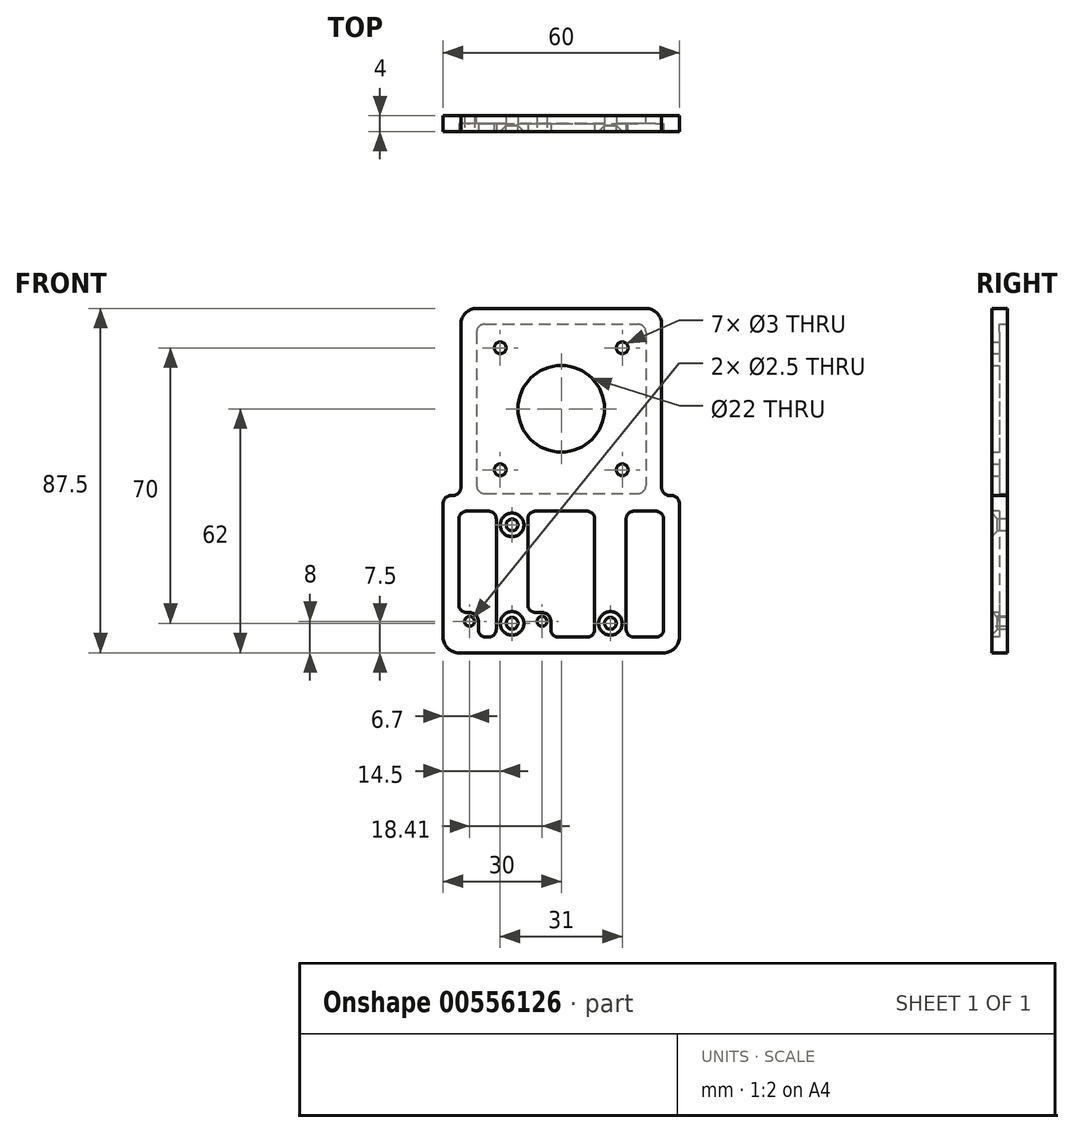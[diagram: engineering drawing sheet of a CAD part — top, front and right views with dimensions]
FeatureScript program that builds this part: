
annotation { "Feature Type Name" : "Feature", "Feature Type Description" : "" }
export const myFeature = defineFeature(function(context is Context, id is Id, definition is map)
    precondition{}
    {
        {
            var Q0;
            Q0=qCreatedBy(makeId("Front.planeOp"),FACE);
            var sketch = newSketch(context, id + "F0", { "sketchPlane" : qUnion([Q0])});
            skPoint(sketch, "E0.middle", {"position": v(0, 0) * mm});
            skLineSegment(sketch, "E1.bottom", {"start": v(21, 41) * mm, "end": v(-21, 41) * mm, "construction": true});
            skLineSegment(sketch, "E1.top", {"start": v(21, -1) * mm, "end": v(-21, -1) * mm, "construction": true});
            skLineSegment(sketch, "E1.left", {"start": v(21, 41) * mm, "end": v(21, -1) * mm, "construction": true});
            skLineSegment(sketch, "E1.right", {"start": v(-21, 41) * mm, "end": v(-21, -1) * mm, "construction": true});
            skPoint(sketch, "E1.middle", {"position": v(0, 20) * mm});
            skLineSegment(sketch, "E2.left", {"start": v(30, -2) * mm, "end": v(30, -42) * mm, "construction": true});
            skLineSegment(sketch, "E2.right", {"start": v(-30, -2) * mm, "end": v(-30, -42) * mm, "construction": true});
            skPoint(sketch, "E2.middle", {"position": v(0, -22) * mm});
            skLineSegment(sketch, "E3", {"start": v(-25.5, -2) * mm, "end": v(-25.5, 45.5) * mm});
            skLineSegment(sketch, "E4", {"start": v(25.5, -2) * mm, "end": v(25.5, 45.5) * mm});
            skLineSegment(sketch, "E5", {"start": v(-25.5, 45.5) * mm, "end": v(25.5, 45.5) * mm});
            skLineSegment(sketch, "E6", {"start": v(-30, -2) * mm, "end": v(-30, -42) * mm});
            skLineSegment(sketch, "E7", {"start": v(30, -42) * mm, "end": v(30, -2) * mm});
            skLineSegment(sketch, "E8", {"start": v(30, -42) * mm, "end": v(-30, -42) * mm});
            skLineSegment(sketch, "E9", {"start": v(-30, -2) * mm, "end": v(30, -2) * mm});
            skSolve(sketch);
        }
        {
            var Q0;
            Q0 = qSketchRegion(id + "F0", true);
            extrude(context, id + "F1", {"entities" : qUnion([Q0]), "depth" : 4 * mm, "offsetDistance" : 25 * mm});
        }
        {
            var Q0;
            Q0=makeQuery(id+"F1.opExtrude","CAP_FACE",FACE,{"disambiguationData":[OSD([sQuery(id+"F0.wireOp",EDGE,"E3"),sQuery(id+"F0.wireOp",EDGE,"E4"),sQuery(id+"F0.wireOp",EDGE,"AjVsnIKu-7JX5-ZN3J-yJHr-BJJlj0IjsVSh"),sQuery(id+"F0.wireOp",EDGE,"zUF1eDCT-iJ0q-WYJ5-TO9I-DUBJJ4F8TYCG"),sQuery(id+"F0.wireOp",EDGE,"R0gw3s5Z-myCC-VoIE-qQNj-JX5kTqaqAvmN"),sQuery(id+"F0.wireOp",EDGE,"0TTXeeu4-dUPo-6RlB-0m7P-MXHo5uVCwiDz"),sQuery(id+"F0.wireOp",EDGE,"BTNMlOGm-kpXo-JoPY-6Hj9-Lp1ODQrAF4Rl"),sQuery(id+"F0.wireOp",EDGE,"W4vJ1xEX-BTs7-1cIY-8ppp-jU2IqAzzoPHu"),sQuery(id+"F0.wireOp",EDGE,"rjm4BpMY-it7c-iU0h-PZAg-QSvS56OCM9jP"),sQuery(id+"F0.wireOp",EDGE,"aUghs46N-WyLj-duN1-bhaf-177DD2MuhRqQ"),sQuery(id+"F0.wireOp",EDGE,"JDqdSihL-KQaK-Av0N-iznf-jRKgxYS6iGmx"),sQuery(id+"F0.wireOp",EDGE,"zwNCGtTh-hdHv-TKGf-VZcB-xR8iGKQpC6Up"),sQuery(id+"F0.wireOp",EDGE,"Ke8YQDsO-ZVhX-azsC-oTJZ-QnQdDkfL8EHA"),sQuery(id+"F0.wireOp",EDGE,"E5"),sQuery(id+"F0.wireOp",EDGE,"p4yK42dh-cCTi-oaBX-tSVU-OnHXovtltKjl"),sQuery(id+"F0.wireOp",EDGE,"P8wBvtXH-8kAn-NcBt-zPsC-BQHUZ9UxVdzU"),sQuery(id+"F0.wireOp",EDGE,"E6"),sQuery(id+"F0.wireOp",EDGE,"E7"),sQuery(id+"F0.wireOp",EDGE,"nOxL5zSL-pdkV-Zte1-GYdC-ii0rABZTziLy"),sQuery(id+"F0.wireOp",EDGE,"9Hkm7kCb-Kjb3-Cx3j-kGQn-9n4TcQlOuVeR")])],"isStart":true});
            var sketch = newSketch(context, id + "F2", { "sketchPlane" : qUnion([Q0])});
            skLineSegment(sketch, "E10.bottom", {"start": v(21.5, 41.5) * mm, "end": v(-21.5, 41.5) * mm});
            skLineSegment(sketch, "E10.top", {"start": v(21.5, -1.5) * mm, "end": v(-21.5, -1.5) * mm});
            skLineSegment(sketch, "E10.left", {"start": v(21.5, 41.5) * mm, "end": v(21.5, -1.5) * mm});
            skLineSegment(sketch, "E10.right", {"start": v(-21.5, 41.5) * mm, "end": v(-21.5, -1.5) * mm});
            skLineSegment(sketch, "E11.bottom", {"start": v(15.5, 35.5) * mm, "end": v(-15.5, 35.5) * mm, "construction": true});
            skLineSegment(sketch, "E11.top", {"start": v(15.5, 4.5) * mm, "end": v(-15.5, 4.5) * mm, "construction": true});
            skLineSegment(sketch, "E11.left", {"start": v(15.5, 35.5) * mm, "end": v(15.5, 4.5) * mm, "construction": true});
            skLineSegment(sketch, "E11.right", {"start": v(-15.5, 35.5) * mm, "end": v(-15.5, 4.5) * mm, "construction": true});
            skPoint(sketch, "E11.middle", {"position": v(0, 20) * mm});
            skCircle(sketch, "E12", {"center": v(0, 20) * mm, "radius": 11 * mm});
            skSolve(sketch);
        }
        {
            var Q0;
            Q0=makeQuery(id+"F2.imprint","IMPRINT",FACE,{"disambiguationData":[TD([[makeQuery(id+"F2.imprint","IMPRINT",EDGE,{"derivedFrom":sQuery(id+"F2.wireOp",EDGE,"E10.bottom")}),1.0]])]});
            extrude(context, id + "F3", {"entities" : qUnion([Q0]), "operationType" : NewBodyOperationType.REMOVE, "oppositeDirection" : true, "depth" : 2 * mm, "offsetDistance" : 25 * mm});
        }
        {
            var Q0;
            Q0=makeQuery(id+"F2.imprint","IMPRINT",FACE,{"disambiguationData":[TD([[makeQuery(id+"F2.imprint","IMPRINT",EDGE,{"derivedFrom":sQuery(id+"F2.wireOp",EDGE,"E12")}),1.0]])]});
            extrude(context, id + "F4", {"entities" : qUnion([Q0]), "operationType" : NewBodyOperationType.REMOVE, "endBound" : BoundingType.THROUGH_ALL, "oppositeDirection" : true, "depth" : 25 * mm, "offsetDistance" : 25 * mm});
        }
        {
            var Q0;
            Q0=sQuery(id+"F2.wireOp",VERTEX,"E11.right.start");
            var Q1;
            Q1=sQuery(id+"F2.wireOp",VERTEX,"E11.left.start");
            var Q2;
            Q2=sQuery(id+"F2.wireOp",VERTEX,"E11.top.start");
            var Q3;
            Q3=sQuery(id+"F2.wireOp",VERTEX,"E11.right.end");
            var Q4;
            Q4=makeQuery(id+"F1.opExtrude","SWEPT_BODY",BODY,{"disambiguationData":[OSD([sQuery(id+"F0.wireOp",EDGE,"E3"),sQuery(id+"F0.wireOp",EDGE,"E4"),sQuery(id+"F0.wireOp",EDGE,"AjVsnIKu-7JX5-ZN3J-yJHr-BJJlj0IjsVSh"),sQuery(id+"F0.wireOp",EDGE,"zUF1eDCT-iJ0q-WYJ5-TO9I-DUBJJ4F8TYCG"),sQuery(id+"F0.wireOp",EDGE,"R0gw3s5Z-myCC-VoIE-qQNj-JX5kTqaqAvmN"),sQuery(id+"F0.wireOp",EDGE,"0TTXeeu4-dUPo-6RlB-0m7P-MXHo5uVCwiDz"),sQuery(id+"F0.wireOp",EDGE,"BTNMlOGm-kpXo-JoPY-6Hj9-Lp1ODQrAF4Rl"),sQuery(id+"F0.wireOp",EDGE,"W4vJ1xEX-BTs7-1cIY-8ppp-jU2IqAzzoPHu"),sQuery(id+"F0.wireOp",EDGE,"rjm4BpMY-it7c-iU0h-PZAg-QSvS56OCM9jP"),sQuery(id+"F0.wireOp",EDGE,"aUghs46N-WyLj-duN1-bhaf-177DD2MuhRqQ"),sQuery(id+"F0.wireOp",EDGE,"JDqdSihL-KQaK-Av0N-iznf-jRKgxYS6iGmx"),sQuery(id+"F0.wireOp",EDGE,"zwNCGtTh-hdHv-TKGf-VZcB-xR8iGKQpC6Up"),sQuery(id+"F0.wireOp",EDGE,"Ke8YQDsO-ZVhX-azsC-oTJZ-QnQdDkfL8EHA"),sQuery(id+"F0.wireOp",EDGE,"E5"),sQuery(id+"F0.wireOp",EDGE,"p4yK42dh-cCTi-oaBX-tSVU-OnHXovtltKjl"),sQuery(id+"F0.wireOp",EDGE,"P8wBvtXH-8kAn-NcBt-zPsC-BQHUZ9UxVdzU"),sQuery(id+"F0.wireOp",EDGE,"E6"),sQuery(id+"F0.wireOp",EDGE,"E7"),sQuery(id+"F0.wireOp",EDGE,"nOxL5zSL-pdkV-Zte1-GYdC-ii0rABZTziLy"),sQuery(id+"F0.wireOp",EDGE,"9Hkm7kCb-Kjb3-Cx3j-kGQn-9n4TcQlOuVeR")])]});
            hole(context, id + "F5", {"style" : HoleStyle.SIMPLE, "endStyle" : HoleEndStyle.THROUGH, "holeDiameter" : 3 * mm, "majorDiameter" : 5 * mm, "isTappedThrough" : true, "tappedDepth" : 12 * mm, "tapClearance" : 3, "locations" : qUnion([Q0, Q1, Q2, Q3]), "scope" : qUnion([Q4])});
        }
        {
            var Q0;
            Q0=makeQuery(id+"F3.boolean.opBoolean","COPY",EDGE,{"derivedFrom":makeQuery(id+"F3.opExtrude","SWEPT_EDGE",EDGE,{"disambiguationData":[OSD([sQuery(id+"F2.wireOp",EDGE,"E10.bottom"),sQuery(id+"F2.wireOp",EDGE,"E10.right")])]})});
            var Q1;
            Q1=makeQuery(id+"F3.boolean.opBoolean","COPY",EDGE,{"derivedFrom":makeQuery(id+"F3.opExtrude","SWEPT_EDGE",EDGE,{"disambiguationData":[OSD([sQuery(id+"F2.wireOp",EDGE,"E10.bottom"),sQuery(id+"F2.wireOp",EDGE,"E10.left")])]})});
            var Q2;
            Q2=makeQuery(id+"F3.boolean.opBoolean","COPY",EDGE,{"derivedFrom":makeQuery(id+"F3.opExtrude","SWEPT_EDGE",EDGE,{"disambiguationData":[OSD([sQuery(id+"F2.wireOp",EDGE,"E10.top"),sQuery(id+"F2.wireOp",EDGE,"E10.left")])]})});
            var Q3;
            Q3=makeQuery(id+"F3.boolean.opBoolean","COPY",EDGE,{"derivedFrom":makeQuery(id+"F3.opExtrude","SWEPT_EDGE",EDGE,{"disambiguationData":[OSD([sQuery(id+"F2.wireOp",EDGE,"E10.top"),sQuery(id+"F2.wireOp",EDGE,"E10.right")])]})});
            fillet(context, id + "F6", {"entities" : qUnion([Q0, Q1, Q2, Q3]), "radius" : 2 * mm, "tangentPropagation" : true, "allowEdgeOverflow" : false});
        }
        {
            var Q0;
            Q0=makeQuery(id+"F1.opExtrude","CAP_FACE",FACE,{"disambiguationData":[OSD([sQuery(id+"F0.wireOp",EDGE,"E3"),sQuery(id+"F0.wireOp",EDGE,"E4"),sQuery(id+"F0.wireOp",EDGE,"AjVsnIKu-7JX5-ZN3J-yJHr-BJJlj0IjsVSh"),sQuery(id+"F0.wireOp",EDGE,"zUF1eDCT-iJ0q-WYJ5-TO9I-DUBJJ4F8TYCG"),sQuery(id+"F0.wireOp",EDGE,"R0gw3s5Z-myCC-VoIE-qQNj-JX5kTqaqAvmN"),sQuery(id+"F0.wireOp",EDGE,"0TTXeeu4-dUPo-6RlB-0m7P-MXHo5uVCwiDz"),sQuery(id+"F0.wireOp",EDGE,"BTNMlOGm-kpXo-JoPY-6Hj9-Lp1ODQrAF4Rl"),sQuery(id+"F0.wireOp",EDGE,"W4vJ1xEX-BTs7-1cIY-8ppp-jU2IqAzzoPHu"),sQuery(id+"F0.wireOp",EDGE,"rjm4BpMY-it7c-iU0h-PZAg-QSvS56OCM9jP"),sQuery(id+"F0.wireOp",EDGE,"aUghs46N-WyLj-duN1-bhaf-177DD2MuhRqQ"),sQuery(id+"F0.wireOp",EDGE,"JDqdSihL-KQaK-Av0N-iznf-jRKgxYS6iGmx"),sQuery(id+"F0.wireOp",EDGE,"zwNCGtTh-hdHv-TKGf-VZcB-xR8iGKQpC6Up"),sQuery(id+"F0.wireOp",EDGE,"Ke8YQDsO-ZVhX-azsC-oTJZ-QnQdDkfL8EHA"),sQuery(id+"F0.wireOp",EDGE,"E5"),sQuery(id+"F0.wireOp",EDGE,"p4yK42dh-cCTi-oaBX-tSVU-OnHXovtltKjl"),sQuery(id+"F0.wireOp",EDGE,"P8wBvtXH-8kAn-NcBt-zPsC-BQHUZ9UxVdzU"),sQuery(id+"F0.wireOp",EDGE,"E6"),sQuery(id+"F0.wireOp",EDGE,"E7"),sQuery(id+"F0.wireOp",EDGE,"nOxL5zSL-pdkV-Zte1-GYdC-ii0rABZTziLy"),sQuery(id+"F0.wireOp",EDGE,"9Hkm7kCb-Kjb3-Cx3j-kGQn-9n4TcQlOuVeR")])],"isStart":false});
            var sketch = newSketch(context, id + "F7", { "sketchPlane" : qUnion([Q0])});
            skLineSegment(sketch, "E13.bottom", {"start": v(-12.5, -9.5) * mm, "end": v(12.5, -9.5) * mm, "construction": true});
            skLineSegment(sketch, "E13.top", {"start": v(12.5, -34.5) * mm, "end": v(-12.5, -34.5) * mm, "construction": true});
            skLineSegment(sketch, "E13.left", {"start": v(12.5, -9.5) * mm, "end": v(12.5, -34.5) * mm, "construction": true});
            skLineSegment(sketch, "E13.right", {"start": v(-12.5, -9.5) * mm, "end": v(-12.5, -34.5) * mm, "construction": true});
            skPoint(sketch, "E13.middle", {"position": v(0, -22) * mm});
            skLineSegment(sketch, "E14.bottom", {"start": v(26, -6) * mm, "end": v(-26, -6) * mm});
            skLineSegment(sketch, "E14.top", {"start": v(26, -38) * mm, "end": v(-26, -38) * mm});
            skLineSegment(sketch, "E14.left", {"start": v(26, -6) * mm, "end": v(26, -38) * mm});
            skLineSegment(sketch, "E14.right", {"start": v(-26, -6) * mm, "end": v(-26, -38) * mm});
            skLineSegment(sketch, "E15", {"start": v(-23.3, -34) * mm, "end": v(-4.9, -34) * mm, "construction": true});
            skCircle(sketch, "E16", {"center": v(-23.3, -34) * mm, "radius": 2.25 * mm});
            skCircle(sketch, "E17", {"center": v(-4.9, -34) * mm, "radius": 2.25 * mm});
            skLineSegment(sketch, "E18", {"start": v(-26, -31.75) * mm, "end": v(-23.3, -31.75) * mm});
            skLineSegment(sketch, "E19", {"start": v(-21.05, -34) * mm, "end": v(-21.05, -38) * mm});
            skLineSegment(sketch, "E20", {"start": v(-2.64, -34) * mm, "end": v(-2.64, -38) * mm});
            skLineSegment(sketch, "E21.bottom", {"start": v(-8.5, -6) * mm, "end": v(-16.5, -6) * mm});
            skLineSegment(sketch, "E21.top", {"start": v(-8.5, -38) * mm, "end": v(-16.5, -38) * mm});
            skLineSegment(sketch, "E21.left", {"start": v(-8.5, -6) * mm, "end": v(-8.5, -38) * mm});
            skLineSegment(sketch, "E21.right", {"start": v(-16.5, -6) * mm, "end": v(-16.5, -38) * mm});
            skPoint(sketch, "E21.middle", {"position": v(-12.5, -22) * mm});
            skLineSegment(sketch, "E22.bottom", {"start": v(16.5, -6) * mm, "end": v(8.5, -6) * mm});
            skLineSegment(sketch, "E22.top", {"start": v(16.5, -38) * mm, "end": v(8.5, -38) * mm});
            skLineSegment(sketch, "E22.left", {"start": v(16.5, -6) * mm, "end": v(16.5, -38) * mm});
            skLineSegment(sketch, "E22.right", {"start": v(8.5, -6) * mm, "end": v(8.5, -38) * mm});
            skPoint(sketch, "E22.middle", {"position": v(12.5, -22) * mm});
            skLineSegment(sketch, "E23", {"start": v(-4.9, -31.75) * mm, "end": v(-8.5, -31.75) * mm});
            skSolve(sketch);
        }
        {
            var Q0;
            {var subQ3=sQuery(id+"F7.wireOp",EDGE,"E18");Q0=makeQuery(id+"F7.imprint","IMPRINT",FACE,{"disambiguationData":[TD([[makeQuery(id+"F7.imprint","IMPRINT",EDGE,{"derivedFrom":subQ3}),1.0]])]});}
            var Q1;
            {var subQ0=sQuery(id+"F7.wireOp",EDGE,"E20");Q1=makeQuery(id+"F7.imprint","IMPRINT",FACE,{"disambiguationData":[TD([[makeQuery(id+"F7.imprint","IMPRINT",EDGE,{"derivedFrom":subQ0}),1.0]])]});}
            var Q2;
            {var subQ0=sQuery(id+"F7.wireOp",EDGE,"E14.left");Q2=makeQuery(id+"F7.imprint","IMPRINT",FACE,{"disambiguationData":[TD([[makeQuery(id+"F7.imprint","IMPRINT",EDGE,{"derivedFrom":subQ0}),-1.0]])]});}
            extrude(context, id + "F8", {"entities" : qUnion([Q0, Q1, Q2]), "operationType" : NewBodyOperationType.REMOVE, "oppositeDirection" : true, "depth" : 2 * mm, "offsetDistance" : 25 * mm});
        }
        {
            var Q0;
            Q0=sQuery(id+"F7.wireOp",VERTEX,"E13.right.start");
            var Q1;
            Q1=sQuery(id+"F7.wireOp",VERTEX,"E13.bottom.start");
            var Q2;
            Q2=sQuery(id+"F7.wireOp",VERTEX,"E13.top.end");
            var Q3;
            Q3=sQuery(id+"F7.wireOp",VERTEX,"E13.left.end");
            var Q4;
            Q4=makeQuery(id+"F1.opExtrude","SWEPT_BODY",BODY,{"disambiguationData":[OSD([sQuery(id+"F0.wireOp",EDGE,"E3"),sQuery(id+"F0.wireOp",EDGE,"E4"),sQuery(id+"F0.wireOp",EDGE,"AjVsnIKu-7JX5-ZN3J-yJHr-BJJlj0IjsVSh"),sQuery(id+"F0.wireOp",EDGE,"zUF1eDCT-iJ0q-WYJ5-TO9I-DUBJJ4F8TYCG"),sQuery(id+"F0.wireOp",EDGE,"R0gw3s5Z-myCC-VoIE-qQNj-JX5kTqaqAvmN"),sQuery(id+"F0.wireOp",EDGE,"0TTXeeu4-dUPo-6RlB-0m7P-MXHo5uVCwiDz"),sQuery(id+"F0.wireOp",EDGE,"BTNMlOGm-kpXo-JoPY-6Hj9-Lp1ODQrAF4Rl"),sQuery(id+"F0.wireOp",EDGE,"W4vJ1xEX-BTs7-1cIY-8ppp-jU2IqAzzoPHu"),sQuery(id+"F0.wireOp",EDGE,"rjm4BpMY-it7c-iU0h-PZAg-QSvS56OCM9jP"),sQuery(id+"F0.wireOp",EDGE,"aUghs46N-WyLj-duN1-bhaf-177DD2MuhRqQ"),sQuery(id+"F0.wireOp",EDGE,"JDqdSihL-KQaK-Av0N-iznf-jRKgxYS6iGmx"),sQuery(id+"F0.wireOp",EDGE,"zwNCGtTh-hdHv-TKGf-VZcB-xR8iGKQpC6Up"),sQuery(id+"F0.wireOp",EDGE,"Ke8YQDsO-ZVhX-azsC-oTJZ-QnQdDkfL8EHA"),sQuery(id+"F0.wireOp",EDGE,"E5"),sQuery(id+"F0.wireOp",EDGE,"p4yK42dh-cCTi-oaBX-tSVU-OnHXovtltKjl"),sQuery(id+"F0.wireOp",EDGE,"P8wBvtXH-8kAn-NcBt-zPsC-BQHUZ9UxVdzU"),sQuery(id+"F0.wireOp",EDGE,"E6"),sQuery(id+"F0.wireOp",EDGE,"E7"),sQuery(id+"F0.wireOp",EDGE,"nOxL5zSL-pdkV-Zte1-GYdC-ii0rABZTziLy"),sQuery(id+"F0.wireOp",EDGE,"9Hkm7kCb-Kjb3-Cx3j-kGQn-9n4TcQlOuVeR")])]});
            hole(context, id + "F9", {"style" : HoleStyle.C_SINK, "endStyle" : HoleEndStyle.THROUGH, "holeDiameter" : 3 * mm, "cSinkDiameter" : 6 * mm, "cSinkAngle" : 90 * degree, "majorDiameter" : 5 * mm, "isTappedThrough" : true, "tappedDepth" : 12 * mm, "tapClearance" : 3, "startFromSketch" : true, "locations" : qUnion([Q0, Q1, Q2, Q3]), "scope" : qUnion([Q4])});
        }
        {
            var Q0;
            Q0=sQuery(id+"F7.wireOp",VERTEX,"E16.center");
            var Q1;
            Q1=sQuery(id+"F7.wireOp",VERTEX,"E15.end");
            var Q2;
            Q2=makeQuery(id+"F1.opExtrude","SWEPT_BODY",BODY,{"disambiguationData":[OSD([sQuery(id+"F0.wireOp",EDGE,"E3"),sQuery(id+"F0.wireOp",EDGE,"E4"),sQuery(id+"F0.wireOp",EDGE,"E5"),sQuery(id+"F0.wireOp",EDGE,"E6"),sQuery(id+"F0.wireOp",EDGE,"E7"),sQuery(id+"F0.wireOp",EDGE,"E8"),sQuery(id+"F0.wireOp",EDGE,"E9")])]});
            hole(context, id + "F10", {"style" : HoleStyle.SIMPLE, "endStyle" : HoleEndStyle.THROUGH, "holeDiameter" : 2.5 * mm, "majorDiameter" : 5 * mm, "isTappedThrough" : true, "tappedDepth" : 12 * mm, "tapClearance" : 3, "locations" : qUnion([Q0, Q1]), "scope" : qUnion([Q2])});
        }
        {
            var Q0;
            Q0=makeQuery(id+"F8.boolean.opBoolean","COPY",EDGE,{"derivedFrom":makeQuery(id+"F8.opExtrude","SWEPT_EDGE",EDGE,{"disambiguationData":[OSD([sQuery(id+"F7.wireOp",EDGE,"E14.bottom"),sQuery(id+"F7.wireOp",EDGE,"E14.right")])]})});
            var Q1;
            Q1=makeQuery(id+"F8.boolean.opBoolean","COPY",EDGE,{"derivedFrom":makeQuery(id+"F8.opExtrude","SWEPT_EDGE",EDGE,{"disambiguationData":[OSD([sQuery(id+"F7.wireOp",EDGE,"E14.bottom"),sQuery(id+"F7.wireOp",EDGE,"E14.left")])]})});
            var Q2;
            Q2=makeQuery(id+"F8.boolean.opBoolean","COPY",EDGE,{"derivedFrom":makeQuery(id+"F8.opExtrude","SWEPT_EDGE",EDGE,{"disambiguationData":[OSD([sQuery(id+"F7.wireOp",EDGE,"E14.top"),sQuery(id+"F7.wireOp",EDGE,"E14.right")])]})});
            var Q3;
            Q3=makeQuery(id+"F8.boolean.opBoolean","COPY",EDGE,{"derivedFrom":makeQuery(id+"F8.opExtrude","SWEPT_EDGE",EDGE,{"disambiguationData":[OSD([sQuery(id+"F7.wireOp",EDGE,"E14.top"),sQuery(id+"F7.wireOp",EDGE,"E14.left")])]})});
            var Q4;
            Q4=makeQuery(id+"F8.boolean.opBoolean","COPY",EDGE,{"derivedFrom":makeQuery(id+"F8.opExtrude","SWEPT_EDGE",EDGE,{"disambiguationData":[OSD([sQuery(id+"F7.wireOp",EDGE,"E14.top"),sQuery(id+"F7.wireOp",EDGE,"E21.top"),sQuery(id+"F7.wireOp",EDGE,"E21.right")])]})});
            var Q5;
            Q5=makeQuery(id+"F8.boolean.opBoolean","COPY",EDGE,{"derivedFrom":makeQuery(id+"F8.opExtrude","SWEPT_EDGE",EDGE,{"disambiguationData":[OSD([sQuery(id+"F7.wireOp",EDGE,"E14.top"),sQuery(id+"F7.wireOp",EDGE,"E22.top"),sQuery(id+"F7.wireOp",EDGE,"E22.right")])]})});
            var Q6;
            Q6=makeQuery(id+"F8.boolean.opBoolean","COPY",EDGE,{"derivedFrom":makeQuery(id+"F8.opExtrude","SWEPT_EDGE",EDGE,{"disambiguationData":[OSD([sQuery(id+"F7.wireOp",EDGE,"E14.bottom"),sQuery(id+"F7.wireOp",EDGE,"E21.bottom"),sQuery(id+"F7.wireOp",EDGE,"E21.right")])]})});
            var Q7;
            Q7=makeQuery(id+"F8.boolean.opBoolean","COPY",EDGE,{"derivedFrom":makeQuery(id+"F8.opExtrude","SWEPT_EDGE",EDGE,{"disambiguationData":[OSD([sQuery(id+"F7.wireOp",EDGE,"E14.bottom"),sQuery(id+"F7.wireOp",EDGE,"E22.bottom"),sQuery(id+"F7.wireOp",EDGE,"E22.right")])]})});
            var Q8;
            Q8=makeQuery(id+"F8.boolean.opBoolean","COPY",EDGE,{"derivedFrom":makeQuery(id+"F8.opExtrude","SWEPT_EDGE",EDGE,{"disambiguationData":[OSD([sQuery(id+"F7.wireOp",EDGE,"E14.bottom"),sQuery(id+"F7.wireOp",EDGE,"E21.bottom"),sQuery(id+"F7.wireOp",EDGE,"E21.left")])]})});
            var Q9;
            Q9=makeQuery(id+"F8.boolean.opBoolean","COPY",EDGE,{"derivedFrom":makeQuery(id+"F8.opExtrude","SWEPT_EDGE",EDGE,{"disambiguationData":[OSD([sQuery(id+"F7.wireOp",EDGE,"E14.bottom"),sQuery(id+"F7.wireOp",EDGE,"E22.bottom"),sQuery(id+"F7.wireOp",EDGE,"E22.left")])]})});
            var Q10;
            Q10=makeQuery(id+"F8.boolean.opBoolean","COPY",EDGE,{"derivedFrom":makeQuery(id+"F8.opExtrude","SWEPT_EDGE",EDGE,{"disambiguationData":[OSD([sQuery(id+"F7.wireOp",EDGE,"E21.left"),sQuery(id+"F7.wireOp",EDGE,"E23")])]})});
            fillet(context, id + "F11", {"entities" : qUnion([Q0, Q1, Q2, Q3, Q4, Q5, Q6, Q7, Q8, Q9, Q10]), "radius" : 2 * mm, "tangentPropagation" : true, "allowEdgeOverflow" : false});
        }
        {
            var Q0;
            Q0=makeQuery(id+"F1.opExtrude","SWEPT_EDGE",EDGE,{"disambiguationData":[OSD([sQuery(id+"F0.wireOp",EDGE,"E4"),sQuery(id+"F0.wireOp",EDGE,"E9")])]});
            var Q1;
            Q1=makeQuery(id+"F1.opExtrude","SWEPT_EDGE",EDGE,{"disambiguationData":[OSD([sQuery(id+"F0.wireOp",EDGE,"E7"),sQuery(id+"F0.wireOp",EDGE,"E9")])]});
            var Q2;
            Q2=makeQuery(id+"F1.opExtrude","SWEPT_EDGE",EDGE,{"disambiguationData":[OSD([sQuery(id+"F0.wireOp",EDGE,"E3"),sQuery(id+"F0.wireOp",EDGE,"E9")])]});
            var Q3;
            Q3=makeQuery(id+"F1.opExtrude","SWEPT_EDGE",EDGE,{"disambiguationData":[OSD([sQuery(id+"F0.wireOp",EDGE,"E6"),sQuery(id+"F0.wireOp",EDGE,"E9")])]});
            fillet(context, id + "F12", {"entities" : qUnion([Q0, Q1, Q2, Q3]), "radius" : 2 * mm, "tangentPropagation" : true, "allowEdgeOverflow" : false});
        }
        {
            var Q0;
            Q0=makeQuery(id+"F1.opExtrude","SWEPT_EDGE",EDGE,{"disambiguationData":[OSD([sQuery(id+"F0.wireOp",EDGE,"E4"),sQuery(id+"F0.wireOp",EDGE,"E5")])]});
            var Q1;
            Q1=makeQuery(id+"F1.opExtrude","SWEPT_EDGE",EDGE,{"disambiguationData":[OSD([sQuery(id+"F0.wireOp",EDGE,"E3"),sQuery(id+"F0.wireOp",EDGE,"E5")])]});
            var Q2;
            Q2=makeQuery(id+"F1.opExtrude","SWEPT_EDGE",EDGE,{"disambiguationData":[OSD([sQuery(id+"F0.wireOp",EDGE,"E6"),sQuery(id+"F0.wireOp",EDGE,"E8")])]});
            var Q3;
            Q3=makeQuery(id+"F1.opExtrude","SWEPT_EDGE",EDGE,{"disambiguationData":[OSD([sQuery(id+"F0.wireOp",EDGE,"E7"),sQuery(id+"F0.wireOp",EDGE,"E8")])]});
            fillet(context, id + "F13", {"entities" : qUnion([Q0, Q1, Q2, Q3]), "radius" : 4 * mm, "tangentPropagation" : true, "allowEdgeOverflow" : false});
        }
    });
